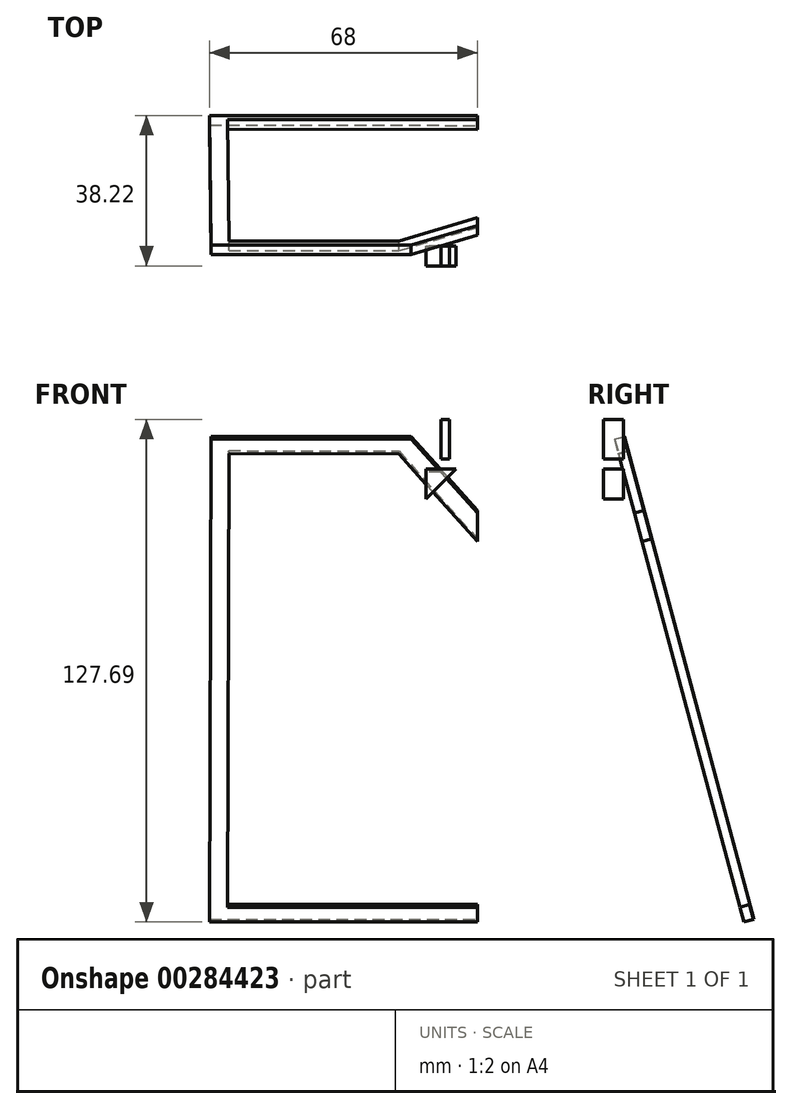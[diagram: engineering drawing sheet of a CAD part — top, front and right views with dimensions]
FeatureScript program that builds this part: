
annotation { "Feature Type Name" : "Feature", "Feature Type Description" : "" }
export const myFeature = defineFeature(function(context is Context, id is Id, definition is map)
    precondition{}
    {
        {
            var Q0;
            Q0=qCreatedBy(makeId("Front.planeOp"),FACE);
            var sketch = newSketch(context, id + "F0", { "sketchPlane" : qUnion([Q0])});
            skLineSegment(sketch, "E0", {"start": v(-3.82, 69.64) * mm, "end": v(-54.62, 69.64) * mm});
            skLineSegment(sketch, "E1", {"start": v(-54.62, 69.64) * mm, "end": v(-55.01, -57.36) * mm});
            skLineSegment(sketch, "E2", {"start": v(-55.01, -57.36) * mm, "end": v(12.98, -57.36) * mm});
            skLineSegment(sketch, "E3", {"start": v(-3.82, 69.64) * mm, "end": v(12.98, 50.24) * mm});
            skLineSegment(sketch, "E4", {"start": v(12.98, -57.36) * mm, "end": v(12.98, -53.46) * mm});
            skLineSegment(sketch, "E5", {"start": v(12.98, -53.46) * mm, "end": v(-50.52, -53.46) * mm});
            skLineSegment(sketch, "E6", {"start": v(-50.52, -53.46) * mm, "end": v(-50.15, 65.91) * mm});
            skLineSegment(sketch, "E7", {"start": v(-50.15, 65.91) * mm, "end": v(-6.97, 65.78) * mm});
            skLineSegment(sketch, "E8", {"start": v(-6.97, 65.78) * mm, "end": v(12.98, 42.74) * mm});
            skLineSegment(sketch, "E9", {"start": v(12.98, 50.24) * mm, "end": v(12.98, 42.74) * mm});
            skSolve(sketch);
        }
        {
            var Q0;
            Q0 = qSketchRegion(id + "F0", true);
            extrude(context, id + "F1", {"entities" : qUnion([Q0]), "endBound" : BoundingType.SYMMETRIC, "depth" : 2.54 * mm});
        }
        {
            var Q0;
            Q0=makeQuery(id+"F1.opExtrude","SWEPT_BODY",BODY,{"disambiguationData":[OSD([sQuery(id+"F0.wireOp",EDGE,"E0"),sQuery(id+"F0.wireOp",EDGE,"E1"),sQuery(id+"F0.wireOp",EDGE,"E2"),sQuery(id+"F0.wireOp",EDGE,"E3"),sQuery(id+"F0.wireOp",EDGE,"E4"),sQuery(id+"F0.wireOp",EDGE,"E5"),sQuery(id+"F0.wireOp",EDGE,"E6"),sQuery(id+"F0.wireOp",EDGE,"E7"),sQuery(id+"F0.wireOp",EDGE,"E8"),sQuery(id+"F0.wireOp",EDGE,"E9")])]});
            var Q1;
            Q1=sQuery(id+"F0.wireOp",EDGE,"E7");
            transform(context, id + "F2", {"entities" : qUnion([Q0]), "transformType" : TransformType.ROTATION, "transformAxis" : qUnion([Q1]), "angle" : 15 * degree, "makeCopy" : false});
        }
        {
            var Q0;
            Q0=qCreatedBy(makeId("Front.planeOp"),FACE);
            var sketch = newSketch(context, id + "F3", { "sketchPlane" : qUnion([Q0])});
            skLineSegment(sketch, "E10", {"start": v(0, 61.58) * mm, "end": v(0, 53.96) * mm});
            skLineSegment(sketch, "E11", {"start": v(0, 53.96) * mm, "end": v(7.62, 61.58) * mm});
            skLineSegment(sketch, "E12", {"start": v(7.62, 61.58) * mm, "end": v(0, 61.58) * mm});
            skText(sketch, "E13", { "text": "I", "fontName": "OpenSans-Bold.ttf"});
            const initialGuessF3  = {"E13": [0.00248, 0.06412, 1, 0, 0.01016]};
            skSetInitialGuess(sketch, initialGuessF3);
            skSolve(sketch);
        }
        {
            var Q0;
            Q0 = qSketchRegion(id + "F3", true);
            extrude(context, id + "F4", {"entities" : qUnion([Q0]), "operationType" : NewBodyOperationType.ADD, "depth" : 5.08 * mm});
        }
    });
